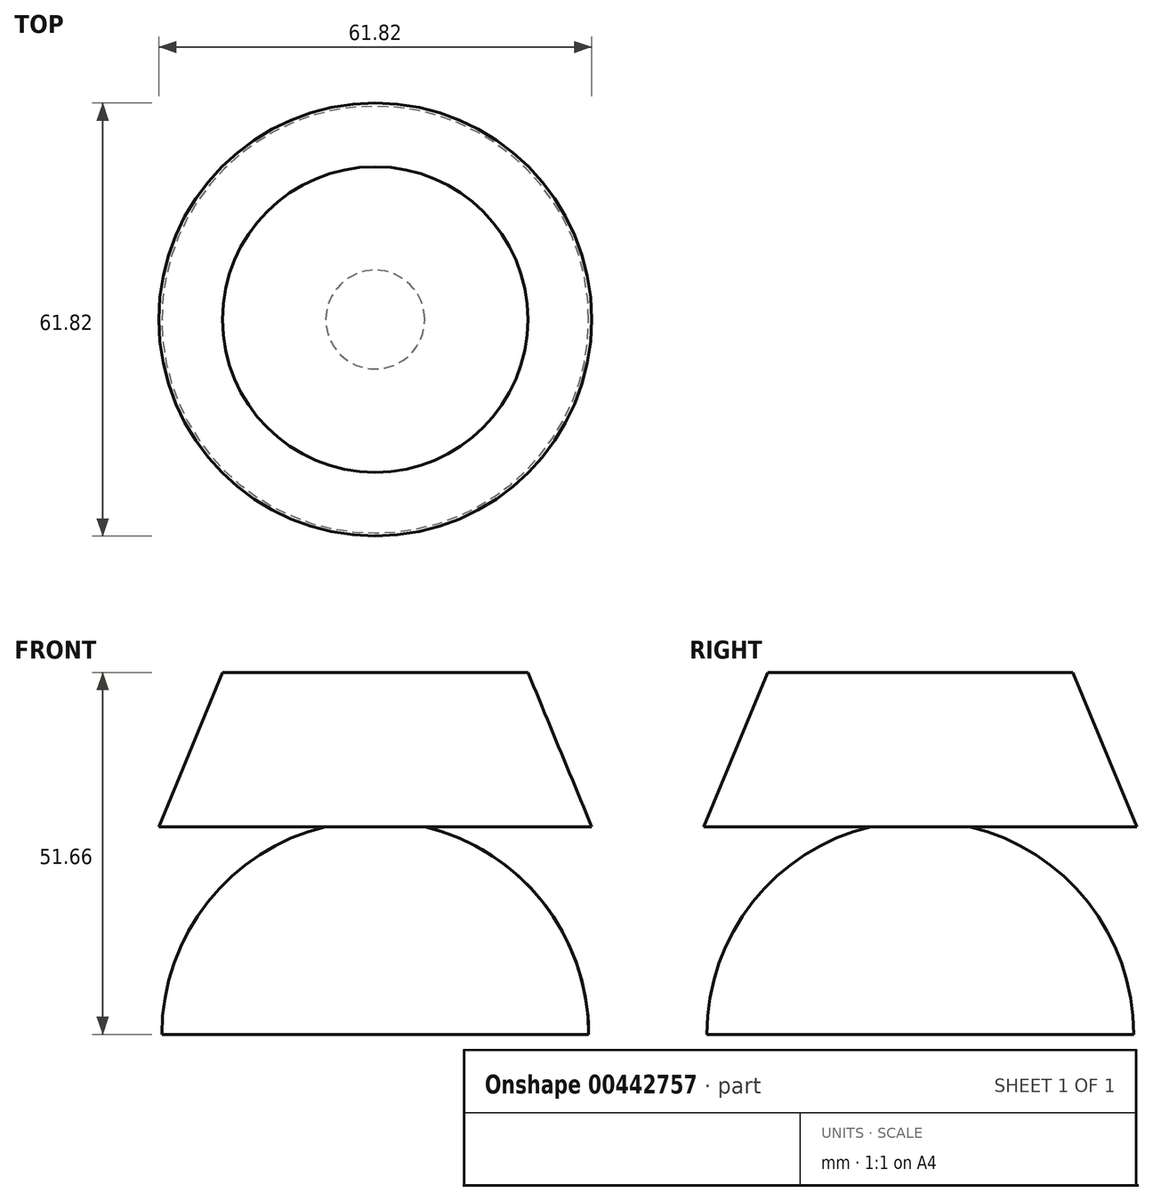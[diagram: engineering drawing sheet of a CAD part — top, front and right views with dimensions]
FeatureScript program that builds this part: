
annotation { "Feature Type Name" : "Feature", "Feature Type Description" : "" }
export const myFeature = defineFeature(function(context is Context, id is Id, definition is map)
    precondition{}
    {
        {
            var Q0;
            Q0=qCreatedBy(makeId("Front.planeOp"),FACE);
            var sketch = newSketch(context, id + "F0", { "sketchPlane" : qUnion([Q0])});
            skLineSegment(sketch, "E0", {"start": v(-21.8, 51.66) * mm, "end": v(0, 51.66) * mm});
            skLineSegment(sketch, "E1", {"start": v(-21.8, 51.66) * mm, "end": v(-30.9, 29.65) * mm});
            skLineSegment(sketch, "E2", {"start": v(-30.9, 29.65) * mm, "end": v(-7.05, 29.65) * mm});
            skArc(sketch, "E3", {"start": v(-7.05, 29.65) * mm, "mid": v(-23.91, 18.9) * mm, "end": v(-30.47, 0) * mm});
            skLineSegment(sketch, "E4", {"start": v(-30.47, 0) * mm, "end": v(0, 0) * mm});
            skPoint(sketch, "E5.orphan", {"position": v(0, 29.65) * mm});
            skLineSegment(sketch, "E6", {"start": v(0, 51.66) * mm, "end": v(0, 0) * mm});
            skSolve(sketch);
        }
        {
            var Q0;
            Q0 = qSketchRegion(id + "F0", true);
            var Q1;
            Q1=sQuery(id+"F0.wireOp",EDGE,"E6");
            revolve(context, id + "F1", {"entities" : qUnion([Q0]), "axis" : qUnion([Q1]), "revolveType" : RevolveType.FULL});
        }
    });
